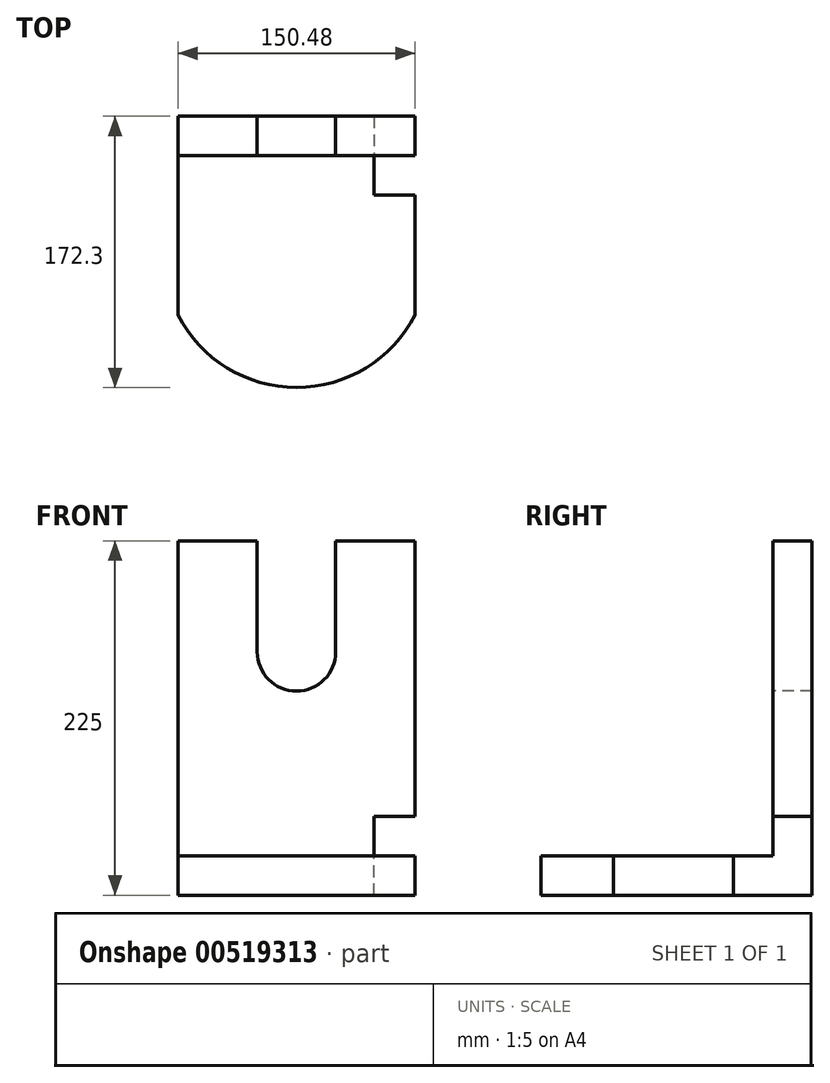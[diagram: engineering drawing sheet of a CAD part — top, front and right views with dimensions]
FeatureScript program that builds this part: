
annotation { "Feature Type Name" : "Feature", "Feature Type Description" : "" }
export const myFeature = defineFeature(function(context is Context, id is Id, definition is map)
    precondition{}
    {
        {
            var Q0;
            Q0=qCreatedBy(makeId("Top.planeOp"),FACE);
            var sketch = newSketch(context, id + "F0", { "sketchPlane" : qUnion([Q0])});
            skArc(sketch, "E0", {"start": v(-75.24, 0) * mm, "mid": v(0, -46.16) * mm, "end": v(75.24, 0) * mm});
            skLineSegment(sketch, "E1", {"start": v(-75.24, 0) * mm, "end": v(-75.24, 126.14) * mm});
            skLineSegment(sketch, "E2", {"start": v(75.24, 0) * mm, "end": v(75.24, 126.14) * mm});
            skLineSegment(sketch, "E3", {"start": v(-75.24, 126.14) * mm, "end": v(75.24, 126.14) * mm});
            skPoint(sketch, "E4.orphan", {"position": v(75.24, 128.63) * mm});
            skSolve(sketch);
        }
        {
            var Q0;
            Q0=makeQuery(id+"F0.imprint","IMPRINT",FACE,{"disambiguationData":[TD([[makeQuery(id+"F0.imprint","IMPRINT",EDGE,{"derivedFrom":sQuery(id+"F0.wireOp",EDGE,"E0")}),1.0]])]});
            extrude(context, id + "F1", {"entities" : qUnion([Q0]), "oppositeDirection" : true, "depth" : 25 * mm, "offsetDistance" : 25 * mm});
        }
        {
            var Q0;
            Q0=makeQuery(id+"F1.opExtrude","CAP_FACE",FACE,{"disambiguationData":[OSD([sQuery(id+"F0.wireOp",EDGE,"E0"),sQuery(id+"F0.wireOp",EDGE,"E1"),sQuery(id+"F0.wireOp",EDGE,"E2"),sQuery(id+"F0.wireOp",EDGE,"E3")])],"isStart":true});
            var sketch = newSketch(context, id + "F2", { "sketchPlane" : qUnion([Q0])});
            skLineSegment(sketch, "E5", {"start": v(-75.24, 101.14) * mm, "end": v(75.24, 101.14) * mm});
            skSolve(sketch);
        }
        {
            var Q0;
            {var subQ0=sQuery(id+"F2.wireOp",EDGE,"E5");Q0=makeQuery(id+"F2.imprint","IMPRINT",FACE,{"disambiguationData":[TD([[makeQuery(id+"F2.imprint","IMPRINT",EDGE,{"derivedFrom":subQ0}),1.0]])]});}
            extrude(context, id + "F3", {"entities" : qUnion([Q0]), "operationType" : NewBodyOperationType.ADD, "depth" : 200 * mm, "offsetDistance" : 25 * mm});
        }
        {
            var Q0;
            Q0=makeQuery(id+"F3.opExtrude","SWEPT_FACE",FACE,{"disambiguationData":[OSD([sQuery(id+"F2.wireOp",EDGE,"E5")])]});
            var sketch = newSketch(context, id + "F4", { "sketchPlane" : qUnion([Q0])});
            skArc(sketch, "E6", {"start": v(-24.94, 129.6) * mm, "mid": v(0, 104.67) * mm, "end": v(24.94, 129.6) * mm});
            skLineSegment(sketch, "E7", {"start": v(-24.94, 129.6) * mm, "end": v(-24.94, 200) * mm});
            skLineSegment(sketch, "E8", {"start": v(24.94, 129.6) * mm, "end": v(24.94, 200) * mm});
            skLineSegment(sketch, "E9", {"start": v(-24.94, 200) * mm, "end": v(24.94, 200) * mm});
            skSolve(sketch);
        }
        {
            var Q0;
            Q0=makeQuery(id+"F4.imprint","IMPRINT",FACE,{"disambiguationData":[TD([[makeQuery(id+"F4.imprint","IMPRINT",EDGE,{"derivedFrom":sQuery(id+"F4.wireOp",EDGE,"E6")}),1.0]])]});
            extrude(context, id + "F5", {"entities" : qUnion([Q0]), "operationType" : NewBodyOperationType.REMOVE, "endBound" : BoundingType.THROUGH_ALL, "oppositeDirection" : true, "depth" : 25 * mm, "offsetDistance" : 25 * mm});
        }
        {
            var Q0;
            {var subQ0=sQuery(id+"F0.wireOp",EDGE,"E2");Q0=makeQuery(id+"F3.boolean.opBoolean","MERGE",FACE,{"derivedFrom":[makeQuery(id+"F1.opExtrude","SWEPT_FACE",FACE,{"disambiguationData":[OSD([subQ0])]}),makeQuery(id+"F3.opExtrude","SWEPT_FACE",FACE,{"disambiguationData":[OSD([subQ0])]})]});}
            var sketch = newSketch(context, id + "F6", { "sketchPlane" : qUnion([Q0])});
            skLineSegment(sketch, "E10.bottom", {"start": v(126.14, -25) * mm, "end": v(76.14, -25) * mm});
            skLineSegment(sketch, "E10.top", {"start": v(126.14, 25) * mm, "end": v(76.14, 25) * mm});
            skLineSegment(sketch, "E10.left", {"start": v(126.14, -25) * mm, "end": v(126.14, 25) * mm});
            skLineSegment(sketch, "E10.right", {"start": v(76.14, -25) * mm, "end": v(76.14, 25) * mm});
            skSolve(sketch);
        }
        {
            var Q0;
            {var subQ1=sQuery(id+"F6.wireOp",EDGE,"E10.bottom");Q0=makeQuery(id+"F6.imprint","IMPRINT",FACE,{"disambiguationData":[TD([[makeQuery(id+"F6.imprint","IMPRINT",EDGE,{"derivedFrom":subQ1}),1.0]])]});}
            extrude(context, id + "F7", {"entities" : qUnion([Q0]), "operationType" : NewBodyOperationType.REMOVE, "oppositeDirection" : true, "depth" : 26 * mm, "offsetDistance" : 25 * mm});
        }
    });
